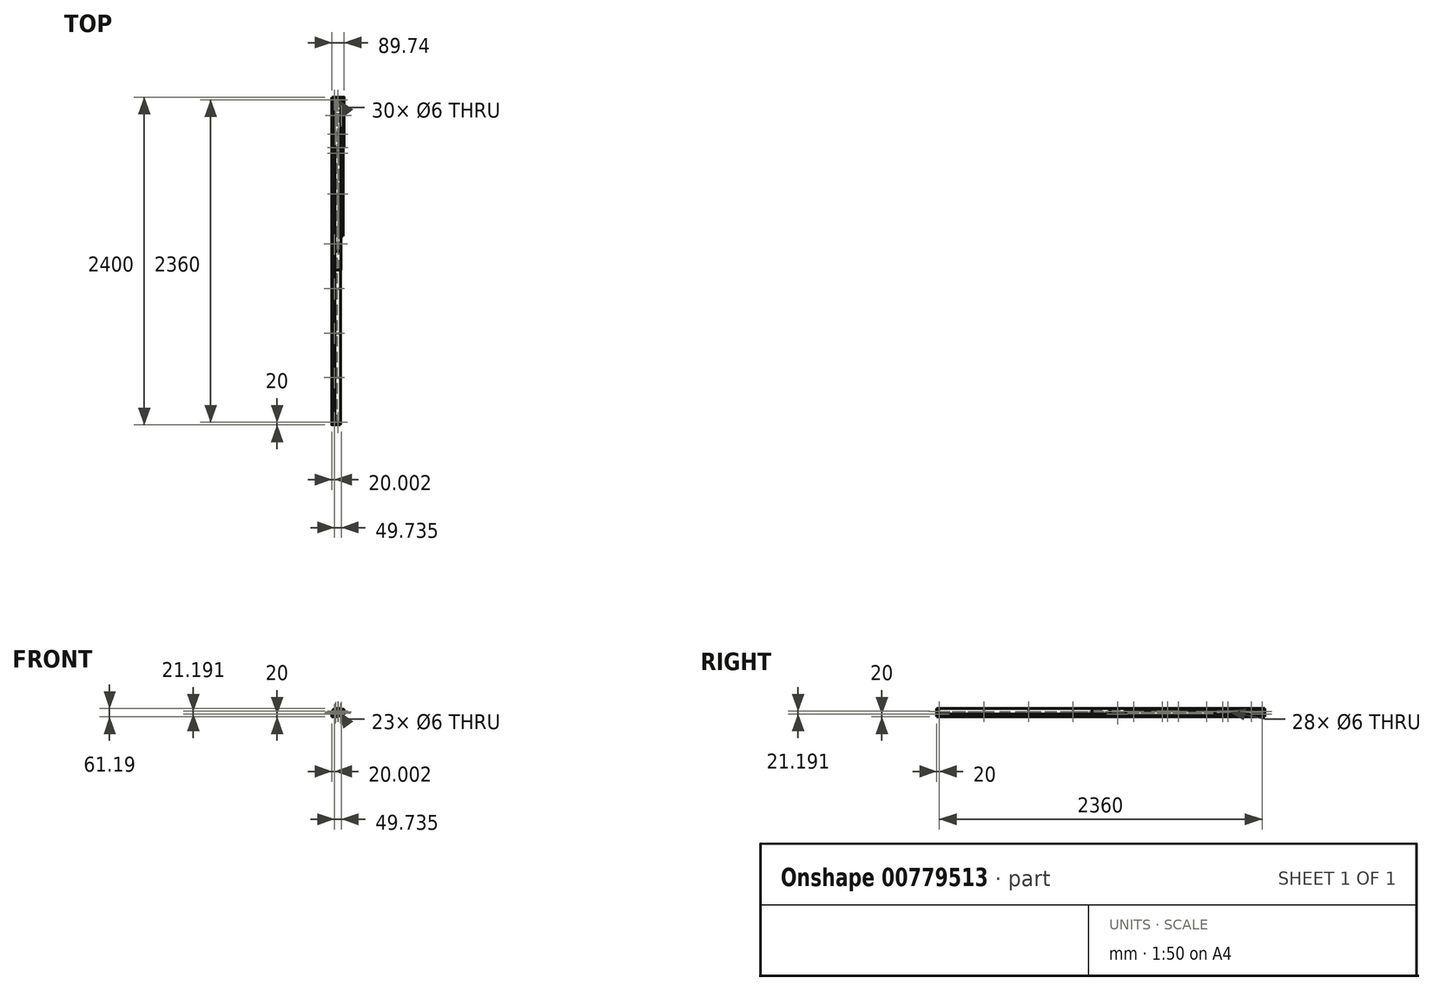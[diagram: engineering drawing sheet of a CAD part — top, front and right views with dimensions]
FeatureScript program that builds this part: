
annotation { "Feature Type Name" : "Feature", "Feature Type Description" : "" }
export const myFeature = defineFeature(function(context is Context, id is Id, definition is map)
    precondition{}
    {
        {
            var Q0;
            Q0=qCreatedBy(makeId("Front.planeOp"),FACE);
            var sketch = newSketch(context, id + "F0", { "sketchPlane" : qUnion([Q0])});
            skLineSegment(sketch, "E0.bottom", {"start": v(-78.72, 40) * mm, "end": v(-38.72, 40) * mm});
            skLineSegment(sketch, "E0.top", {"start": v(-78.72, 0) * mm, "end": v(-38.72, 0) * mm});
            skLineSegment(sketch, "E0.left", {"start": v(-78.72, 40) * mm, "end": v(-78.72, 0) * mm});
            skLineSegment(sketch, "E0.right", {"start": v(-38.72, 40) * mm, "end": v(-38.72, 0) * mm});
            skSolve(sketch);
        }
        {
            var Q0;
            Q0=makeQuery(id+"F0.imprint","IMPRINT",FACE,{"disambiguationData":[TD([[makeQuery(id+"F0.imprint","IMPRINT",EDGE,{"derivedFrom":sQuery(id+"F0.wireOp",EDGE,"E0.bottom")}),-1.0]])]});
            extrude(context, id + "F1", {"entities" : qUnion([Q0]), "depth" : 2400 * mm, "offsetDistance" : 25 * mm});
        }
        {
            var Q0;
            Q0=makeQuery(id+"F1.opExtrude","SWEPT_EDGE",EDGE,{"disambiguationData":[OSD([sQuery(id+"F0.wireOp",EDGE,"E0.bottom"),sQuery(id+"F0.wireOp",EDGE,"E0.left")])]});
            var Q1;
            Q1=makeQuery(id+"F1.opExtrude","SWEPT_EDGE",EDGE,{"disambiguationData":[OSD([sQuery(id+"F0.wireOp",EDGE,"E0.bottom"),sQuery(id+"F0.wireOp",EDGE,"E0.right")])]});
            var Q2;
            Q2=makeQuery(id+"F1.opExtrude","SWEPT_EDGE",EDGE,{"disambiguationData":[OSD([sQuery(id+"F0.wireOp",EDGE,"E0.top"),sQuery(id+"F0.wireOp",EDGE,"E0.right")])]});
            var Q3;
            Q3=makeQuery(id+"F1.opExtrude","SWEPT_EDGE",EDGE,{"disambiguationData":[OSD([sQuery(id+"F0.wireOp",EDGE,"E0.top"),sQuery(id+"F0.wireOp",EDGE,"E0.left")])]});
            fillet(context, id + "F2", {"entities" : qUnion([Q0, Q1, Q2, Q3]), "radius" : 5 * mm, "tangentPropagation" : true, "allowEdgeOverflow" : false});
        }
        {
            var Q0;
            Q0=makeQuery(id+"F1.opExtrude","CAP_FACE",FACE,{"disambiguationData":[OSD([sQuery(id+"F0.wireOp",EDGE,"E0.bottom"),sQuery(id+"F0.wireOp",EDGE,"E0.top"),sQuery(id+"F0.wireOp",EDGE,"E0.left"),sQuery(id+"F0.wireOp",EDGE,"E0.right")])],"isStart":false});
            var sketch = newSketch(context, id + "F3", { "sketchPlane" : qUnion([Q0])});
            skPoint(sketch, "E1", {"position": v(-58.72, 20) * mm});
            skSolve(sketch);
        }
        {
            var Q0;
            Q0=makeQuery(id+"F1.opExtrude","SWEPT_FACE",FACE,{"disambiguationData":[OSD([sQuery(id+"F0.wireOp",EDGE,"E0.bottom")])]});
            var sketch = newSketch(context, id + "F4", { "sketchPlane" : qUnion([Q0])});
            skPoint(sketch, "E2", {"position": v(-58.72, -20) * mm});
            skPoint(sketch, "E3", {"position": v(-58.72, -1076) * mm});
            skPoint(sketch, "E4", {"position": v(-58.72, -2380) * mm});
            skPoint(sketch, "E4.positionSnap0", {"position": v(-58.72, -2400) * mm});
            skPoint(sketch, "E5", {"position": v(-58.72, -2054) * mm});
            skPoint(sketch, "E6", {"position": v(-58.72, -1728) * mm});
            skPoint(sketch, "E7", {"position": v(-58.72, -1402) * mm});
            skSolve(sketch);
        }
        {
            var Q0;
            Q0=makeQuery(id+"F1.opExtrude","SWEPT_FACE",FACE,{"disambiguationData":[OSD([sQuery(id+"F0.wireOp",EDGE,"E0.right")])]});
            var sketch = newSketch(context, id + "F5", { "sketchPlane" : qUnion([Q0])});
            skPoint(sketch, "E8", {"position": v(-2380, 20) * mm});
            skPoint(sketch, "E9", {"position": v(-1076, 20) * mm});
            skPoint(sketch, "E10", {"position": v(-20, 20) * mm});
            skSolve(sketch);
        }
        {
            var Q0;
            Q0=sQuery(id+"F5.wireOp",VERTEX,"E10");
            var Q1;
            Q1=sQuery(id+"F4.wireOp",VERTEX,"E2");
            var Q2;
            Q2=sQuery(id+"F5.wireOp",VERTEX,"E9");
            var Q3;
            Q3=sQuery(id+"F4.wireOp",VERTEX,"E3");
            var Q4;
            Q4=sQuery(id+"F4.wireOp",VERTEX,"E7");
            var Q5;
            Q5=sQuery(id+"F4.wireOp",VERTEX,"E6");
            var Q6;
            Q6=sQuery(id+"F4.wireOp",VERTEX,"E5");
            var Q7;
            Q7=sQuery(id+"F5.wireOp",VERTEX,"E8");
            var Q8;
            Q8=sQuery(id+"F4.wireOp",VERTEX,"E4");
            var Q9;
            Q9=sQuery(id+"F3.wireOp",VERTEX,"E1");
            var Q10;
            Q10=makeQuery(id+"F1.opExtrude","SWEPT_BODY",BODY,{"disambiguationData":[OSD([sQuery(id+"F0.wireOp",EDGE,"E0.bottom"),sQuery(id+"F0.wireOp",EDGE,"E0.top"),sQuery(id+"F0.wireOp",EDGE,"E0.left"),sQuery(id+"F0.wireOp",EDGE,"E0.right")])]});
            hole(context, id + "F6", {"style" : HoleStyle.SIMPLE, "endStyle" : HoleEndStyle.THROUGH, "holeDiameter" : 6 * mm, "majorDiameter" : 5 * mm, "isTappedThrough" : true, "tappedDepth" : 12 * mm, "tapClearance" : 3, "locations" : qUnion([Q0, Q1, Q2, Q3, Q4, Q5, Q6, Q7, Q8, Q9]), "scope" : qUnion([Q10])});
        }
        {
            var Q0;
            Q0=qCreatedBy(makeId("Front.planeOp"),FACE);
            var sketch = newSketch(context, id + "F7", { "sketchPlane" : qUnion([Q0])});
            skLineSegment(sketch, "E11.bottom", {"start": v(-53.74, 60.85) * mm, "end": v(-13.74, 60.85) * mm});
            skLineSegment(sketch, "E11.top", {"start": v(-53.74, 20.85) * mm, "end": v(-13.74, 20.85) * mm});
            skLineSegment(sketch, "E11.left", {"start": v(-53.74, 60.85) * mm, "end": v(-53.74, 20.85) * mm});
            skLineSegment(sketch, "E11.right", {"start": v(-13.74, 60.85) * mm, "end": v(-13.74, 20.85) * mm});
            skSolve(sketch);
        }
        {
            var Q0;
            Q0=makeQuery(id+"F7.imprint","IMPRINT",FACE,{"disambiguationData":[TD([[makeQuery(id+"F7.imprint","IMPRINT",EDGE,{"derivedFrom":sQuery(id+"F7.wireOp",EDGE,"E11.bottom")}),-1.0]])]});
            extrude(context, id + "F8", {"entities" : qUnion([Q0]), "depth" : 365 * mm, "offsetDistance" : 25 * mm});
        }
        {
            var Q0;
            Q0=makeQuery(id+"F8.opExtrude","SWEPT_EDGE",EDGE,{"disambiguationData":[OSD([sQuery(id+"F7.wireOp",EDGE,"E11.bottom"),sQuery(id+"F7.wireOp",EDGE,"E11.left")])]});
            var Q1;
            Q1=makeQuery(id+"F8.opExtrude","SWEPT_EDGE",EDGE,{"disambiguationData":[OSD([sQuery(id+"F7.wireOp",EDGE,"E11.bottom"),sQuery(id+"F7.wireOp",EDGE,"E11.right")])]});
            var Q2;
            Q2=makeQuery(id+"F8.opExtrude","SWEPT_EDGE",EDGE,{"disambiguationData":[OSD([sQuery(id+"F7.wireOp",EDGE,"E11.top"),sQuery(id+"F7.wireOp",EDGE,"E11.right")])]});
            var Q3;
            Q3=makeQuery(id+"F8.opExtrude","SWEPT_EDGE",EDGE,{"disambiguationData":[OSD([sQuery(id+"F7.wireOp",EDGE,"E11.top"),sQuery(id+"F7.wireOp",EDGE,"E11.left")])]});
            fillet(context, id + "F9", {"entities" : qUnion([Q0, Q1, Q2, Q3]), "radius" : 5 * mm, "tangentPropagation" : true, "allowEdgeOverflow" : false});
        }
        {
            var Q0;
            Q0=makeQuery(id+"F8.opExtrude","CAP_FACE",FACE,{"disambiguationData":[OSD([sQuery(id+"F7.wireOp",EDGE,"E11.bottom"),sQuery(id+"F7.wireOp",EDGE,"E11.top"),sQuery(id+"F7.wireOp",EDGE,"E11.left"),sQuery(id+"F7.wireOp",EDGE,"E11.right")])],"isStart":false});
            var sketch = newSketch(context, id + "F10", { "sketchPlane" : qUnion([Q0])});
            skPoint(sketch, "E12", {"position": v(-33.74, 40.85) * mm});
            skPoint(sketch, "E12.positionSnap0", {"position": v(-53.74, 40.85) * mm});
            skPoint(sketch, "E12.positionSnap1", {"position": v(-33.74, 60.85) * mm});
            skSolve(sketch);
        }
        {
            var Q0;
            Q0=sQuery(id+"F10.wireOp",VERTEX,"E12");
            var Q1;
            Q1=makeQuery(id+"F8.opExtrude","SWEPT_BODY",BODY,{"disambiguationData":[OSD([sQuery(id+"F7.wireOp",EDGE,"E11.bottom"),sQuery(id+"F7.wireOp",EDGE,"E11.top"),sQuery(id+"F7.wireOp",EDGE,"E11.left"),sQuery(id+"F7.wireOp",EDGE,"E11.right")])]});
            hole(context, id + "F11", {"style" : HoleStyle.SIMPLE, "endStyle" : HoleEndStyle.THROUGH, "holeDiameter" : 6 * mm, "majorDiameter" : 5 * mm, "isTappedThrough" : true, "tappedDepth" : 12 * mm, "tapClearance" : 3, "locations" : qUnion([Q0]), "scope" : qUnion([Q1])});
        }
        {
            var Q0;
            Q0=qCreatedBy(makeId("Front.planeOp"),FACE);
            var sketch = newSketch(context, id + "F12", { "sketchPlane" : qUnion([Q0])});
            skLineSegment(sketch, "E13.bottom", {"start": v(-52, 61.2) * mm, "end": v(-12, 61.2) * mm});
            skLineSegment(sketch, "E13.top", {"start": v(-52, 21.2) * mm, "end": v(-12, 21.2) * mm});
            skLineSegment(sketch, "E13.left", {"start": v(-52, 61.2) * mm, "end": v(-52, 21.2) * mm});
            skLineSegment(sketch, "E13.right", {"start": v(-12, 61.2) * mm, "end": v(-12, 21.2) * mm});
            skSolve(sketch);
        }
        {
            var Q0;
            Q0=makeQuery(id+"F12.imprint","IMPRINT",FACE,{"disambiguationData":[TD([[makeQuery(id+"F12.imprint","IMPRINT",EDGE,{"derivedFrom":sQuery(id+"F12.wireOp",EDGE,"E13.bottom")}),-1.0]])]});
            extrude(context, id + "F13", {"entities" : qUnion([Q0]), "depth" : 1130 * mm, "offsetDistance" : 25 * mm});
        }
        {
            var Q0;
            Q0=makeQuery(id+"F13.opExtrude","SWEPT_EDGE",EDGE,{"disambiguationData":[OSD([sQuery(id+"F12.wireOp",EDGE,"E13.bottom"),sQuery(id+"F12.wireOp",EDGE,"E13.left")])]});
            var Q1;
            Q1=makeQuery(id+"F13.opExtrude","SWEPT_EDGE",EDGE,{"disambiguationData":[OSD([sQuery(id+"F12.wireOp",EDGE,"E13.bottom"),sQuery(id+"F12.wireOp",EDGE,"E13.right")])]});
            var Q2;
            Q2=makeQuery(id+"F13.opExtrude","SWEPT_EDGE",EDGE,{"disambiguationData":[OSD([sQuery(id+"F12.wireOp",EDGE,"E13.top"),sQuery(id+"F12.wireOp",EDGE,"E13.right")])]});
            var Q3;
            Q3=makeQuery(id+"F13.opExtrude","SWEPT_EDGE",EDGE,{"disambiguationData":[OSD([sQuery(id+"F12.wireOp",EDGE,"E13.top"),sQuery(id+"F12.wireOp",EDGE,"E13.left")])]});
            fillet(context, id + "F14", {"entities" : qUnion([Q0, Q1, Q2, Q3]), "radius" : 5 * mm, "tangentPropagation" : true, "allowEdgeOverflow" : false});
        }
        {
            var Q0;
            Q0=makeQuery(id+"F13.opExtrude","CAP_FACE",FACE,{"disambiguationData":[OSD([sQuery(id+"F12.wireOp",EDGE,"E13.bottom"),sQuery(id+"F12.wireOp",EDGE,"E13.top"),sQuery(id+"F12.wireOp",EDGE,"E13.left"),sQuery(id+"F12.wireOp",EDGE,"E13.right")])],"isStart":false});
            var sketch = newSketch(context, id + "F15", { "sketchPlane" : qUnion([Q0])});
            skPoint(sketch, "E14", {"position": v(-32, 41.2) * mm});
            skPoint(sketch, "E14.positionSnap0", {"position": v(-52, 41.2) * mm});
            skPoint(sketch, "E14.positionSnap1", {"position": v(-32, 61.2) * mm});
            skSolve(sketch);
        }
        {
            var Q0;
            Q0=makeQuery(id+"F13.opExtrude","SWEPT_FACE",FACE,{"disambiguationData":[OSD([sQuery(id+"F12.wireOp",EDGE,"E13.bottom")])]});
            var sketch = newSketch(context, id + "F16", { "sketchPlane" : qUnion([Q0])});
            skPoint(sketch, "E15", {"position": v(-32, -710) * mm});
            skPoint(sketch, "E16", {"position": v(-32, -270) * mm});
            skPoint(sketch, "E17", {"position": v(-32, -370) * mm});
            skPoint(sketch, "E18", {"position": v(-32, -410) * mm});
            skSolve(sketch);
        }
        {
            var Q0;
            Q0=makeQuery(id+"F13.opExtrude","SWEPT_FACE",FACE,{"disambiguationData":[OSD([sQuery(id+"F12.wireOp",EDGE,"E13.right")])]});
            var sketch = newSketch(context, id + "F17", { "sketchPlane" : qUnion([Q0])});
            skPoint(sketch, "E19", {"position": v(-710, 41.2) * mm});
            skPoint(sketch, "E20", {"position": v(-270, 41.2) * mm});
            skSolve(sketch);
        }
        {
            var Q0;
            Q0=sQuery(id+"F16.wireOp",VERTEX,"E16");
            var Q1;
            Q1=sQuery(id+"F17.wireOp",VERTEX,"E20");
            var Q2;
            Q2=sQuery(id+"F16.wireOp",VERTEX,"E15");
            var Q3;
            Q3=sQuery(id+"F17.wireOp",VERTEX,"E19");
            var Q4;
            Q4=sQuery(id+"F15.wireOp",VERTEX,"E14");
            var Q5;
            Q5=sQuery(id+"F16.wireOp",VERTEX,"E17");
            var Q6;
            Q6=sQuery(id+"F16.wireOp",VERTEX,"E18");
            var Q7;
            Q7=makeQuery(id+"F13.opExtrude","SWEPT_BODY",BODY,{"disambiguationData":[OSD([sQuery(id+"F12.wireOp",EDGE,"E13.bottom"),sQuery(id+"F12.wireOp",EDGE,"E13.top"),sQuery(id+"F12.wireOp",EDGE,"E13.left"),sQuery(id+"F12.wireOp",EDGE,"E13.right")])]});
            hole(context, id + "F18", {"style" : HoleStyle.SIMPLE, "endStyle" : HoleEndStyle.THROUGH, "holeDiameter" : 6 * mm, "majorDiameter" : 5 * mm, "isTappedThrough" : true, "tappedDepth" : 12 * mm, "tapClearance" : 3, "locations" : qUnion([Q0, Q1, Q2, Q3, Q4, Q5, Q6]), "scope" : qUnion([Q7])});
        }
        {
            var Q0;
            Q0=qCreatedBy(makeId("Front.planeOp"),FACE);
            var sketch = newSketch(context, id + "F19", { "sketchPlane" : qUnion([Q0])});
            skLineSegment(sketch, "E21.bottom", {"start": v(-54.95, 59.94) * mm, "end": v(-14.95, 59.94) * mm});
            skLineSegment(sketch, "E21.top", {"start": v(-54.95, 19.94) * mm, "end": v(-14.95, 19.94) * mm});
            skLineSegment(sketch, "E21.left", {"start": v(-54.95, 59.94) * mm, "end": v(-54.95, 19.94) * mm});
            skLineSegment(sketch, "E21.right", {"start": v(-14.95, 59.94) * mm, "end": v(-14.95, 19.94) * mm});
            skSolve(sketch);
        }
        {
            var Q0;
            Q0=makeQuery(id+"F19.imprint","IMPRINT",FACE,{"disambiguationData":[TD([[makeQuery(id+"F19.imprint","IMPRINT",EDGE,{"derivedFrom":sQuery(id+"F19.wireOp",EDGE,"E21.bottom")}),-1.0]])]});
            extrude(context, id + "F20", {"entities" : qUnion([Q0]), "depth" : 2400 * mm, "offsetDistance" : 25 * mm});
        }
        {
            var Q0;
            Q0=makeQuery(id+"F20.opExtrude","SWEPT_EDGE",EDGE,{"disambiguationData":[OSD([sQuery(id+"F19.wireOp",EDGE,"E21.bottom"),sQuery(id+"F19.wireOp",EDGE,"E21.left")])]});
            var Q1;
            Q1=makeQuery(id+"F20.opExtrude","SWEPT_EDGE",EDGE,{"disambiguationData":[OSD([sQuery(id+"F19.wireOp",EDGE,"E21.bottom"),sQuery(id+"F19.wireOp",EDGE,"E21.right")])]});
            var Q2;
            Q2=makeQuery(id+"F20.opExtrude","SWEPT_EDGE",EDGE,{"disambiguationData":[OSD([sQuery(id+"F19.wireOp",EDGE,"E21.top"),sQuery(id+"F19.wireOp",EDGE,"E21.right")])]});
            var Q3;
            Q3=makeQuery(id+"F20.opExtrude","SWEPT_EDGE",EDGE,{"disambiguationData":[OSD([sQuery(id+"F19.wireOp",EDGE,"E21.top"),sQuery(id+"F19.wireOp",EDGE,"E21.left")])]});
            fillet(context, id + "F21", {"entities" : qUnion([Q0, Q1, Q2, Q3]), "radius" : 5 * mm, "tangentPropagation" : true, "allowEdgeOverflow" : false});
        }
        {
            var Q0;
            Q0=makeQuery(id+"F20.opExtrude","SWEPT_FACE",FACE,{"disambiguationData":[OSD([sQuery(id+"F19.wireOp",EDGE,"E21.right")])]});
            var sketch = newSketch(context, id + "F22", { "sketchPlane" : qUnion([Q0])});
            skPoint(sketch, "E22", {"position": v(-2054, 39.94) * mm});
            skPoint(sketch, "E23", {"position": v(-1728, 39.94) * mm});
            skPoint(sketch, "E24", {"position": v(-1402, 39.94) * mm});
            skPoint(sketch, "E25", {"position": v(-1076, 39.94) * mm});
            skPoint(sketch, "E26", {"position": v(-750, 39.94) * mm});
            skPoint(sketch, "E27", {"position": v(-424, 39.94) * mm});
            skPoint(sketch, "E28", {"position": v(-98, 39.94) * mm});
            skPoint(sketch, "E29", {"position": v(-20, 39.94) * mm});
            skPoint(sketch, "E30", {"position": v(-2380, 39.94) * mm});
            skSolve(sketch);
        }
        {
            var Q0;
            Q0=makeQuery(id+"F20.opExtrude","SWEPT_FACE",FACE,{"disambiguationData":[OSD([sQuery(id+"F19.wireOp",EDGE,"E21.bottom")])]});
            var sketch = newSketch(context, id + "F23", { "sketchPlane" : qUnion([Q0])});
            skPoint(sketch, "E31", {"position": v(-34.95, -20) * mm});
            skPoint(sketch, "E32", {"position": v(-34.95, -2380) * mm});
            skPoint(sketch, "E33", {"position": v(-34.95, -1076) * mm});
            skSolve(sketch);
        }
        {
            var Q0;
            Q0=sQuery(id+"F22.wireOp",VERTEX,"E30");
            var Q1;
            Q1=sQuery(id+"F23.wireOp",VERTEX,"E32");
            var Q2;
            Q2=sQuery(id+"F22.wireOp",VERTEX,"E22");
            var Q3;
            Q3=sQuery(id+"F22.wireOp",VERTEX,"E23");
            var Q4;
            Q4=sQuery(id+"F22.wireOp",VERTEX,"E24");
            var Q5;
            Q5=sQuery(id+"F22.wireOp",VERTEX,"E25");
            var Q6;
            Q6=sQuery(id+"F23.wireOp",VERTEX,"E33");
            var Q7;
            Q7=sQuery(id+"F22.wireOp",VERTEX,"E26");
            var Q8;
            Q8=sQuery(id+"F22.wireOp",VERTEX,"E27");
            var Q9;
            Q9=sQuery(id+"F22.wireOp",VERTEX,"E28");
            var Q10;
            Q10=sQuery(id+"F22.wireOp",VERTEX,"E29");
            var Q11;
            Q11=sQuery(id+"F23.wireOp",VERTEX,"E31");
            var Q12;
            Q12=makeQuery(id+"F20.opExtrude","SWEPT_BODY",BODY,{"disambiguationData":[OSD([sQuery(id+"F19.wireOp",EDGE,"E21.bottom"),sQuery(id+"F19.wireOp",EDGE,"E21.top"),sQuery(id+"F19.wireOp",EDGE,"E21.left"),sQuery(id+"F19.wireOp",EDGE,"E21.right")])]});
            hole(context, id + "F24", {"style" : HoleStyle.SIMPLE, "endStyle" : HoleEndStyle.THROUGH, "holeDiameter" : 6 * mm, "majorDiameter" : 5 * mm, "isTappedThrough" : true, "tappedDepth" : 12 * mm, "tapClearance" : 3, "locations" : qUnion([Q0, Q1, Q2, Q3, Q4, Q5, Q6, Q7, Q8, Q9, Q10, Q11]), "scope" : qUnion([Q12])});
        }
        {
            var Q0;
            Q0=qCreatedBy(makeId("Front.planeOp"),FACE);
            var sketch = newSketch(context, id + "F25", { "sketchPlane" : qUnion([Q0])});
            skLineSegment(sketch, "E34.bottom", {"start": v(-52, 60.13) * mm, "end": v(-12, 60.13) * mm});
            skLineSegment(sketch, "E34.top", {"start": v(-52, 20.13) * mm, "end": v(-12, 20.13) * mm});
            skLineSegment(sketch, "E34.left", {"start": v(-52, 60.13) * mm, "end": v(-52, 20.13) * mm});
            skLineSegment(sketch, "E34.right", {"start": v(-12, 60.13) * mm, "end": v(-12, 20.13) * mm});
            skSolve(sketch);
        }
        {
            var Q0;
            Q0=makeQuery(id+"F25.imprint","IMPRINT",FACE,{"disambiguationData":[TD([[makeQuery(id+"F25.imprint","IMPRINT",EDGE,{"derivedFrom":sQuery(id+"F25.wireOp",EDGE,"E34.bottom")}),-1.0]])]});
            extrude(context, id + "F26", {"entities" : qUnion([Q0]), "depth" : 1264 * mm, "offsetDistance" : 25 * mm});
        }
        {
            var Q0;
            Q0=makeQuery(id+"F26.opExtrude","SWEPT_EDGE",EDGE,{"disambiguationData":[OSD([sQuery(id+"F25.wireOp",EDGE,"E34.bottom"),sQuery(id+"F25.wireOp",EDGE,"E34.right")])]});
            var Q1;
            Q1=makeQuery(id+"F26.opExtrude","SWEPT_EDGE",EDGE,{"disambiguationData":[OSD([sQuery(id+"F25.wireOp",EDGE,"E34.top"),sQuery(id+"F25.wireOp",EDGE,"E34.right")])]});
            var Q2;
            Q2=makeQuery(id+"F26.opExtrude","SWEPT_EDGE",EDGE,{"disambiguationData":[OSD([sQuery(id+"F25.wireOp",EDGE,"E34.top"),sQuery(id+"F25.wireOp",EDGE,"E34.left")])]});
            var Q3;
            Q3=makeQuery(id+"F26.opExtrude","SWEPT_EDGE",EDGE,{"disambiguationData":[OSD([sQuery(id+"F25.wireOp",EDGE,"E34.bottom"),sQuery(id+"F25.wireOp",EDGE,"E34.left")])]});
            fillet(context, id + "F27", {"entities" : qUnion([Q0, Q1, Q2, Q3]), "radius" : 5 * mm, "tangentPropagation" : true, "allowEdgeOverflow" : false});
        }
        {
            var Q0;
            Q0=makeQuery(id+"F26.opExtrude","CAP_FACE",FACE,{"disambiguationData":[OSD([sQuery(id+"F25.wireOp",EDGE,"E34.bottom"),sQuery(id+"F25.wireOp",EDGE,"E34.top"),sQuery(id+"F25.wireOp",EDGE,"E34.left"),sQuery(id+"F25.wireOp",EDGE,"E34.right")])],"isStart":false});
            var sketch = newSketch(context, id + "F28", { "sketchPlane" : qUnion([Q0])});
            skPoint(sketch, "E35", {"position": v(-32, 40.13) * mm});
            skPoint(sketch, "E35.positionSnap0", {"position": v(-52, 40.13) * mm});
            skPoint(sketch, "E35.positionSnap1", {"position": v(-32, 60.13) * mm});
            skSolve(sketch);
        }
        {
            var Q0;
            Q0=makeQuery(id+"F26.opExtrude","SWEPT_FACE",FACE,{"disambiguationData":[OSD([sQuery(id+"F25.wireOp",EDGE,"E34.right")])]});
            var sketch = newSketch(context, id + "F29", { "sketchPlane" : qUnion([Q0])});
            skPoint(sketch, "E36", {"position": v(-958, 40.13) * mm});
            skPoint(sketch, "E36.positionSnap0", {"position": v(-1264, 40.13) * mm});
            skPoint(sketch, "E37", {"position": v(-632, 40.13) * mm});
            skPoint(sketch, "E38", {"position": v(-306, 40.13) * mm});
            skSolve(sketch);
        }
        {
            var Q0;
            Q0=sQuery(id+"F28.wireOp",VERTEX,"E35");
            var Q1;
            Q1=sQuery(id+"F29.wireOp",VERTEX,"E36");
            var Q2;
            Q2=sQuery(id+"F29.wireOp",VERTEX,"E37");
            var Q3;
            Q3=sQuery(id+"F29.wireOp",VERTEX,"E38");
            var Q4;
            Q4=makeQuery(id+"F26.opExtrude","SWEPT_BODY",BODY,{"disambiguationData":[OSD([sQuery(id+"F25.wireOp",EDGE,"E34.bottom"),sQuery(id+"F25.wireOp",EDGE,"E34.top"),sQuery(id+"F25.wireOp",EDGE,"E34.left"),sQuery(id+"F25.wireOp",EDGE,"E34.right")])]});
            hole(context, id + "F30", {"style" : HoleStyle.SIMPLE, "endStyle" : HoleEndStyle.THROUGH, "holeDiameter" : 6 * mm, "majorDiameter" : 5 * mm, "isTappedThrough" : true, "tappedDepth" : 12 * mm, "tapClearance" : 3, "locations" : qUnion([Q0, Q1, Q2, Q3]), "scope" : qUnion([Q4])});
        }
        {
            var Q0;
            Q0=qCreatedBy(makeId("Front.planeOp"),FACE);
            var sketch = newSketch(context, id + "F31", { "sketchPlane" : qUnion([Q0])});
            skLineSegment(sketch, "E39.bottom", {"start": v(-68.98, 56.2) * mm, "end": v(11.02, 56.2) * mm});
            skLineSegment(sketch, "E39.top", {"start": v(-68.98, 16.2) * mm, "end": v(11.02, 16.2) * mm});
            skLineSegment(sketch, "E39.left", {"start": v(-68.98, 56.2) * mm, "end": v(-68.98, 16.2) * mm});
            skLineSegment(sketch, "E39.right", {"start": v(11.02, 56.2) * mm, "end": v(11.02, 16.2) * mm});
            skSolve(sketch);
        }
        {
            var Q0;
            Q0=makeQuery(id+"F31.imprint","IMPRINT",FACE,{"disambiguationData":[TD([[makeQuery(id+"F31.imprint","IMPRINT",EDGE,{"derivedFrom":sQuery(id+"F31.wireOp",EDGE,"E39.bottom")}),-1.0]])]});
            extrude(context, id + "F32", {"entities" : qUnion([Q0]), "depth" : 365 * mm, "offsetDistance" : 25 * mm});
        }
        {
            var Q0;
            Q0=makeQuery(id+"F32.opExtrude","SWEPT_EDGE",EDGE,{"disambiguationData":[OSD([sQuery(id+"F31.wireOp",EDGE,"E39.bottom"),sQuery(id+"F31.wireOp",EDGE,"E39.left")])]});
            var Q1;
            Q1=makeQuery(id+"F32.opExtrude","SWEPT_EDGE",EDGE,{"disambiguationData":[OSD([sQuery(id+"F31.wireOp",EDGE,"E39.bottom"),sQuery(id+"F31.wireOp",EDGE,"E39.right")])]});
            var Q2;
            Q2=makeQuery(id+"F32.opExtrude","SWEPT_EDGE",EDGE,{"disambiguationData":[OSD([sQuery(id+"F31.wireOp",EDGE,"E39.top"),sQuery(id+"F31.wireOp",EDGE,"E39.right")])]});
            var Q3;
            Q3=makeQuery(id+"F32.opExtrude","SWEPT_EDGE",EDGE,{"disambiguationData":[OSD([sQuery(id+"F31.wireOp",EDGE,"E39.top"),sQuery(id+"F31.wireOp",EDGE,"E39.left")])]});
            fillet(context, id + "F33", {"entities" : qUnion([Q0, Q1, Q2, Q3]), "radius" : 5 * mm, "tangentPropagation" : true, "allowEdgeOverflow" : false});
        }
        {
            var Q0;
            Q0=makeQuery(id+"F32.opExtrude","CAP_FACE",FACE,{"disambiguationData":[OSD([sQuery(id+"F31.wireOp",EDGE,"E39.bottom"),sQuery(id+"F31.wireOp",EDGE,"E39.top"),sQuery(id+"F31.wireOp",EDGE,"E39.left"),sQuery(id+"F31.wireOp",EDGE,"E39.right")])],"isStart":false});
            var sketch = newSketch(context, id + "F34", { "sketchPlane" : qUnion([Q0])});
            skPoint(sketch, "E40", {"position": v(-48.98, 36.2) * mm});
            skPoint(sketch, "E40.positionSnap0", {"position": v(-68.98, 36.2) * mm});
            skPoint(sketch, "E41", {"position": v(-8.98, 36.2) * mm});
            skSolve(sketch);
        }
        {
            var Q0;
            Q0=makeQuery(id+"F32.opExtrude","SWEPT_FACE",FACE,{"disambiguationData":[OSD([sQuery(id+"F31.wireOp",EDGE,"E39.bottom")])]});
            var sketch = newSketch(context, id + "F35", { "sketchPlane" : qUnion([Q0])});
            skPoint(sketch, "E42", {"position": v(-48.98, -135) * mm});
            skPoint(sketch, "E43", {"position": v(-8.98, -135) * mm});
            skSolve(sketch);
        }
        {
            var Q0;
            Q0=sQuery(id+"F35.wireOp",VERTEX,"E42");
            var Q1;
            Q1=sQuery(id+"F35.wireOp",VERTEX,"E43");
            var Q2;
            Q2=sQuery(id+"F34.wireOp",VERTEX,"E40");
            var Q3;
            Q3=sQuery(id+"F34.wireOp",VERTEX,"E41");
            var Q4;
            Q4=makeQuery(id+"F32.opExtrude","SWEPT_BODY",BODY,{"disambiguationData":[OSD([sQuery(id+"F31.wireOp",EDGE,"E39.bottom"),sQuery(id+"F31.wireOp",EDGE,"E39.top"),sQuery(id+"F31.wireOp",EDGE,"E39.left"),sQuery(id+"F31.wireOp",EDGE,"E39.right")])]});
            hole(context, id + "F36", {"style" : HoleStyle.SIMPLE, "endStyle" : HoleEndStyle.THROUGH, "holeDiameter" : 6 * mm, "majorDiameter" : 5 * mm, "isTappedThrough" : true, "tappedDepth" : 12 * mm, "tapClearance" : 3, "locations" : qUnion([Q0, Q1, Q2, Q3]), "scope" : qUnion([Q4])});
        }
        {
            var Q0;
            Q0=qCreatedBy(makeId("Front.planeOp"),FACE);
            var sketch = newSketch(context, id + "F37", { "sketchPlane" : qUnion([Q0])});
            skLineSegment(sketch, "E44.bottom", {"start": v(-74.59, 47.49) * mm, "end": v(5.41, 47.49) * mm});
            skLineSegment(sketch, "E44.top", {"start": v(-74.59, 7.49) * mm, "end": v(5.41, 7.49) * mm});
            skLineSegment(sketch, "E44.left", {"start": v(-74.59, 47.49) * mm, "end": v(-74.59, 7.49) * mm});
            skLineSegment(sketch, "E44.right", {"start": v(5.41, 47.49) * mm, "end": v(5.41, 7.49) * mm});
            skSolve(sketch);
        }
        {
            var Q0;
            Q0=makeQuery(id+"F37.imprint","IMPRINT",FACE,{"disambiguationData":[TD([[makeQuery(id+"F37.imprint","IMPRINT",EDGE,{"derivedFrom":sQuery(id+"F37.wireOp",EDGE,"E44.bottom")}),-1.0]])]});
            extrude(context, id + "F38", {"entities" : qUnion([Q0]), "depth" : 1016 * mm, "offsetDistance" : 25 * mm});
        }
        {
            var Q0;
            Q0=makeQuery(id+"F38.opExtrude","SWEPT_EDGE",EDGE,{"disambiguationData":[OSD([sQuery(id+"F37.wireOp",EDGE,"E44.bottom"),sQuery(id+"F37.wireOp",EDGE,"E44.left")])]});
            var Q1;
            Q1=makeQuery(id+"F38.opExtrude","SWEPT_EDGE",EDGE,{"disambiguationData":[OSD([sQuery(id+"F37.wireOp",EDGE,"E44.bottom"),sQuery(id+"F37.wireOp",EDGE,"E44.right")])]});
            var Q2;
            Q2=makeQuery(id+"F38.opExtrude","SWEPT_EDGE",EDGE,{"disambiguationData":[OSD([sQuery(id+"F37.wireOp",EDGE,"E44.top"),sQuery(id+"F37.wireOp",EDGE,"E44.right")])]});
            var Q3;
            Q3=makeQuery(id+"F38.opExtrude","SWEPT_EDGE",EDGE,{"disambiguationData":[OSD([sQuery(id+"F37.wireOp",EDGE,"E44.top"),sQuery(id+"F37.wireOp",EDGE,"E44.left")])]});
            fillet(context, id + "F39", {"entities" : qUnion([Q0, Q1, Q2, Q3]), "radius" : 5 * mm, "tangentPropagation" : true, "allowEdgeOverflow" : false});
        }
        {
            var Q0;
            Q0=makeQuery(id+"F38.opExtrude","CAP_FACE",FACE,{"disambiguationData":[OSD([sQuery(id+"F37.wireOp",EDGE,"E44.bottom"),sQuery(id+"F37.wireOp",EDGE,"E44.top"),sQuery(id+"F37.wireOp",EDGE,"E44.left"),sQuery(id+"F37.wireOp",EDGE,"E44.right")])],"isStart":false});
            var sketch = newSketch(context, id + "F40", { "sketchPlane" : qUnion([Q0])});
            skPoint(sketch, "E45", {"position": v(-54.59, 27.49) * mm});
            skPoint(sketch, "E45.positionSnap0", {"position": v(-74.59, 27.49) * mm});
            skPoint(sketch, "E46", {"position": v(-14.59, 27.49) * mm});
            skSolve(sketch);
        }
        {
            var Q0;
            Q0=sQuery(id+"F40.wireOp",VERTEX,"E45");
            var Q1;
            Q1=sQuery(id+"F40.wireOp",VERTEX,"E46");
            var Q2;
            Q2=makeQuery(id+"F38.opExtrude","SWEPT_BODY",BODY,{"disambiguationData":[OSD([sQuery(id+"F37.wireOp",EDGE,"E44.bottom"),sQuery(id+"F37.wireOp",EDGE,"E44.top"),sQuery(id+"F37.wireOp",EDGE,"E44.left"),sQuery(id+"F37.wireOp",EDGE,"E44.right")])]});
            hole(context, id + "F41", {"style" : HoleStyle.SIMPLE, "endStyle" : HoleEndStyle.THROUGH, "holeDiameter" : 6 * mm, "majorDiameter" : 5 * mm, "isTappedThrough" : true, "tappedDepth" : 12 * mm, "tapClearance" : 3, "locations" : qUnion([Q0, Q1]), "scope" : qUnion([Q2])});
        }
    });
